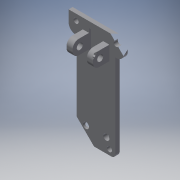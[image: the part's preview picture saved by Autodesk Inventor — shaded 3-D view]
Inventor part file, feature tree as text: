
AUTODESK INVENTOR PART (.ipt)
format: ipt  version: 2016 (Build 200138000, 138)  size: 199,168 bytes
history: native  units: mm
features: extrude x5, sketch x5, fillet x1
ambient origin geometry x8: Origin, YZ Plane, XZ Plane, XY Plane, X Axis, Y Axis, Z Axis, Center Point
bodies: Solid1 (feature_tree)
feature tree (11):
  extrude  "Extrusion1"  Depth=2.0mm TaperAngle=0.0deg
  extrude  "Extrusion2"  Depth=3.0mm
  fillet  "Fillet1"  Radius=7.0mm
  extrude  "Extrusion4"  Depth=3.0mm
  extrude  "Extrusion5"  Depth=5.0mm
  extrude  "Extrusion6"  Depth=2.0mm
  sketch  "Sketch1"  dims[d6=3.5mm d7=1.0mm d8=1.0mm d9=3.5mm d10=0.0mm d11=2.5mm d12=1.0mm d13=2.0mm d14=0.0mm]
  sketch  "Sketch2"  dims[d15=7.0mm d18=3.0mm d21=7.0mm]
  sketch  "Sketch4"  dims[d22=8.0mm d23=0.0mm d24=3.0mm]
  sketch  "Sketch5"  dims[d32=3.0mm d36=5.0mm]
  sketch  "Sketch6"  dims[d37=2.0mm d38=2.0mm d39=1.0mm d40=0.0mm d41=3.0mm d42=3.0mm d43=4.5mm d44=3.5mm d45=3.5mm d46=15.0mm d47=0.0mm d48=3.0mm d49=5.0mm d50=3.0mm d51=0.0mm d52=7.0mm]
